# Revit family: AFX-Rusnak-LED_Ceiling
name_source: partatom
category: Lighting Fixtures
units: mm (PartAtom-declared; Revit-internal decimal feet)

## family parameters
Cut with Voids When Loaded = No
Host = Face
Light Source = Yes
Part Type = Normal
Room Calculation Point = No
Round Connector Dimension = Use Diameter
Shared = No

## types (1)
- RSKF1616L30D1BK
    Apparent Load = 0 VA
    Assembly Code = D5020200
    Body Finish = AFX - Black Steel
    Cap Finish = AFX - Black Steel
    Color Filter = 16777215
    Colour Rendering Index = 90
    Default Elevation = 48"
    Description = LED Ceiling - 8"H x 15 1/2"Dia
    Diameter = 15 1/2"
    Diffuser Finish = AFX - White Acrylic
    Dimming Lamp Color Temperature Shift = <None>
    Emit Shape Visible in Rendering = No
    Emit from Circle Diameter = 14"
    Height = 8"
    Housing Finish = AFX - Black Steel
    Keynote = 12500
    Manufacturer = AFX Inc
    Model = RSKF1616L30D1BK
    Photometric Web File = RSKF1616L30D1PC.IES
    Product Documentation Link = https://www.afxinc.com
    Revit File Built By = https://servex-us.com
    Sustainability = https://lamprecycle.org
    Tilt Angle = -90.00°
    Type Comments = Rusnak
    URL = https://www.afxinc.com
    Voltage = 120 V
    Wattage Comments = 25W

## geometry (parser evidence)
native form markers: Sweep x2
no freeform markers — native parametric forms only
